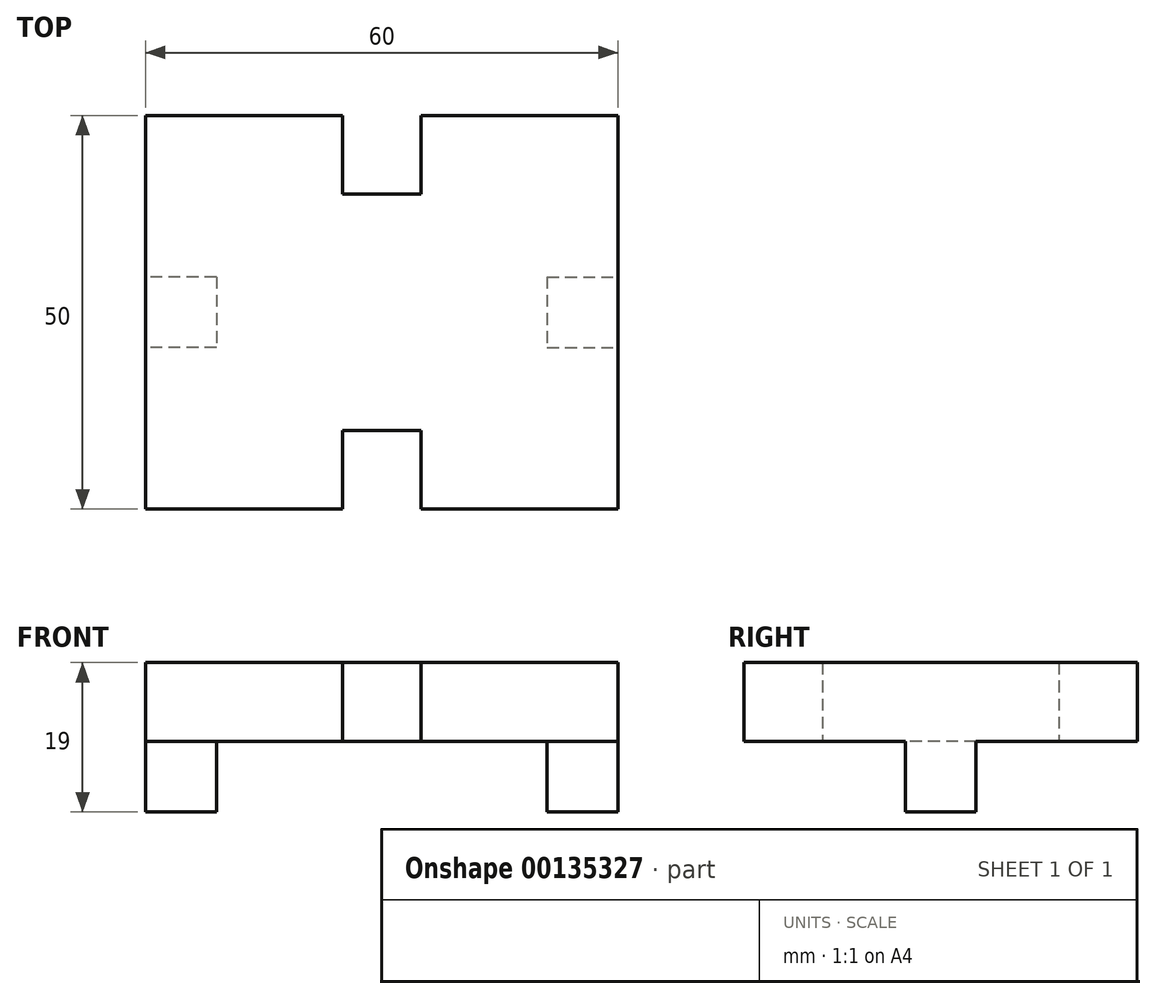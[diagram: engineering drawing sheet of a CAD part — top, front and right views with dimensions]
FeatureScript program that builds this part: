
annotation { "Feature Type Name" : "Feature", "Feature Type Description" : "" }
export const myFeature = defineFeature(function(context is Context, id is Id, definition is map)
    precondition{}
    {
        {
            var Q0;
            Q0=qCreatedBy(makeId("Top.planeOp"),FACE);
            var sketch = newSketch(context, id + "F0", { "sketchPlane" : qUnion([Q0])});
            skLineSegment(sketch, "E0.bottom", {"start": v(80.72, 58.96) * mm, "end": v(55.72, 58.96) * mm});
            skLineSegment(sketch, "E0.top", {"start": v(80.72, 8.96) * mm, "end": v(55.72, 8.96) * mm});
            skLineSegment(sketch, "E0.left", {"start": v(80.72, 58.96) * mm, "end": v(80.72, 8.96) * mm});
            skLineSegment(sketch, "E0.right", {"start": v(20.72, 58.96) * mm, "end": v(20.72, 8.96) * mm});
            skLineSegment(sketch, "E1.top", {"start": v(55.72, 48.96) * mm, "end": v(45.72, 48.96) * mm});
            skLineSegment(sketch, "E1.left", {"start": v(55.72, 58.96) * mm, "end": v(55.72, 48.96) * mm});
            skLineSegment(sketch, "E1.right", {"start": v(45.72, 58.96) * mm, "end": v(45.72, 48.96) * mm});
            skLineSegment(sketch, "E2.top", {"start": v(55.72, 18.96) * mm, "end": v(45.72, 18.96) * mm});
            skLineSegment(sketch, "E2.left", {"start": v(55.72, 8.96) * mm, "end": v(55.72, 18.96) * mm});
            skLineSegment(sketch, "E2.right", {"start": v(45.72, 8.96) * mm, "end": v(45.72, 18.96) * mm});
            skLineSegment(sketch, "E3.trimOffspring", {"start": v(45.72, 8.96) * mm, "end": v(20.72, 8.96) * mm});
            skLineSegment(sketch, "E4.trimOffspring", {"start": v(45.72, 58.96) * mm, "end": v(20.72, 58.96) * mm});
            skSolve(sketch);
        }
        {
            var Q0;
            Q0=makeQuery(id+"F0.imprint","IMPRINT",FACE,{"disambiguationData":[TD([[makeQuery(id+"F0.imprint","IMPRINT",EDGE,{"derivedFrom":sQuery(id+"F0.wireOp",EDGE,"E0.bottom")}),1.0]])]});
            extrude(context, id + "F1", {"entities" : qUnion([Q0]), "depth" : 10 * mm});
        }
        {
            var Q0;
            Q0=makeQuery(id+"F0.imprint","IMPRINT",FACE,{"disambiguationData":[TD([[makeQuery(id+"F0.imprint","IMPRINT",EDGE,{"derivedFrom":sQuery(id+"F0.wireOp",EDGE,"E0.bottom")}),1.0]])]});
            var sketch = newSketch(context, id + "F2", { "sketchPlane" : qUnion([Q0])});
            skLineSegment(sketch, "E5.right", {"start": v(29.72, 38.46) * mm, "end": v(29.72, 29.46) * mm});
            skLineSegment(sketch, "E6", {"start": v(29.72, 29.46) * mm, "end": v(20.72, 29.46) * mm});
            skLineSegment(sketch, "E7", {"start": v(29.72, 38.46) * mm, "end": v(20.72, 38.46) * mm});
            skLineSegment(sketch, "E8", {"start": v(50.72, 18.96) * mm, "end": v(50.72, 48.96) * mm, "construction": true});
            skLineSegment(sketch, "E9.MirrorCS", {"start": v(71.72, 29.46) * mm, "end": v(80.72, 29.46) * mm});
            skLineSegment(sketch, "E10.MirrorCS", {"start": v(71.72, 38.46) * mm, "end": v(80.72, 38.46) * mm});
            skLineSegment(sketch, "E11.MirrorCS", {"start": v(71.72, 38.46) * mm, "end": v(71.72, 29.46) * mm});
            skPoint(sketch, "E12.orphan", {"position": v(50.72, 55.6) * mm});
            skLineSegment(sketch, "E13.0", {"start": v(55.72, 48.96) * mm, "end": v(45.72, 48.96) * mm});
            skPoint(sketch, "E14.orphan", {"position": v(50.72, 37.28) * mm});
            skLineSegment(sketch, "E15.0", {"start": v(80.72, 58.96) * mm, "end": v(80.72, 8.96) * mm});
            skLineSegment(sketch, "E16.0", {"start": v(20.72, 58.96) * mm, "end": v(20.72, 8.96) * mm});
            skSolve(sketch);
        }
        {
            var Q0;
            Q0 = qSketchRegion(id + "F2", true);
            extrude(context, id + "F3", {"entities" : qUnion([Q0]), "operationType" : NewBodyOperationType.ADD, "oppositeDirection" : true, "depth" : 9 * mm});
        }
    });
